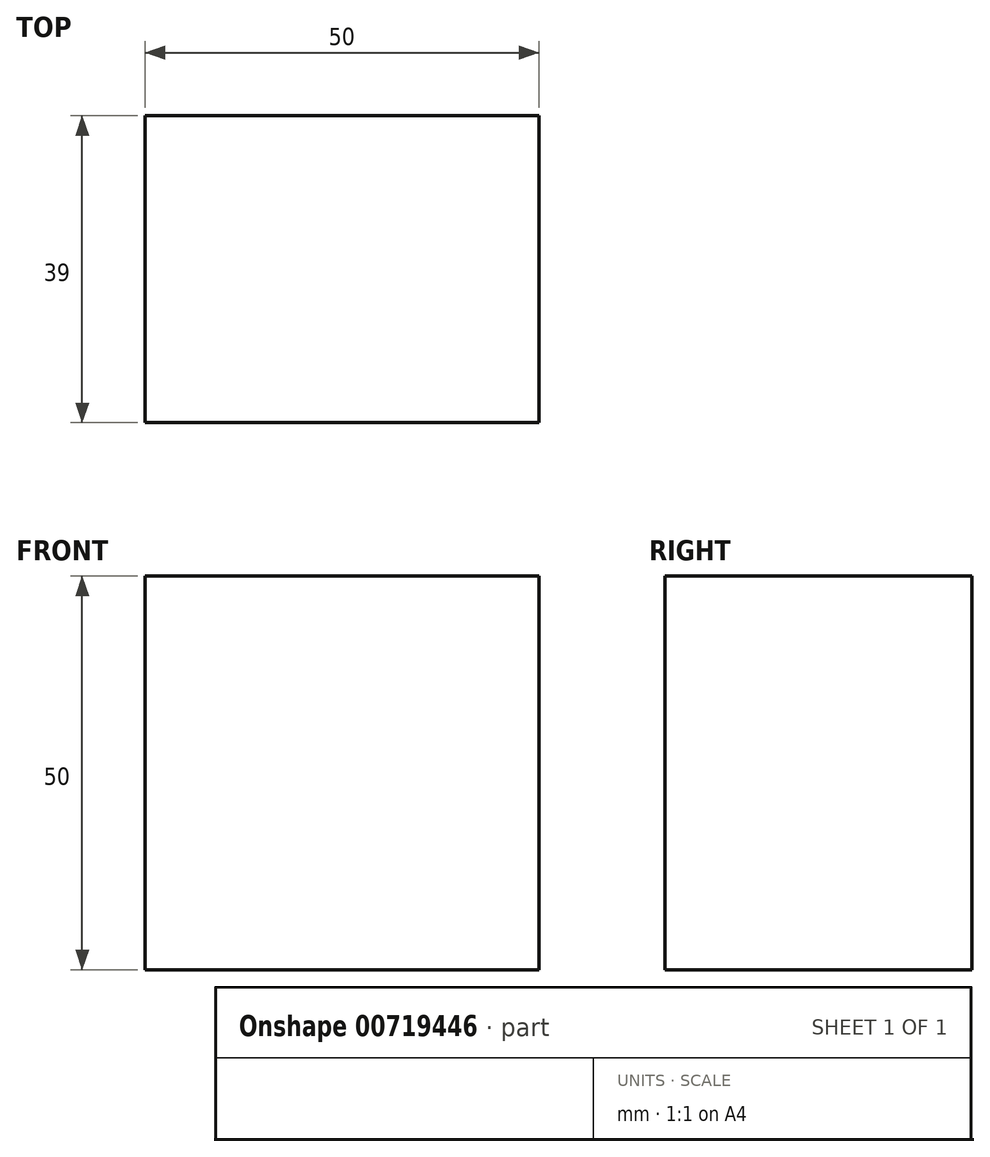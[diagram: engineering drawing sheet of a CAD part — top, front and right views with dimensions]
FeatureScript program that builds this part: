
annotation { "Feature Type Name" : "Feature", "Feature Type Description" : "" }
export const myFeature = defineFeature(function(context is Context, id is Id, definition is map)
    precondition{}
    {
        {
            var Q0;
            Q0=qCreatedBy(makeId("Front.planeOp"),FACE);
            var sketch = newSketch(context, id + "F0", { "sketchPlane" : qUnion([Q0])});
            skLineSegment(sketch, "E0.bottom", {"start": v(-25, 25) * mm, "end": v(25, 25) * mm});
            skLineSegment(sketch, "E0.top", {"start": v(-25, -25) * mm, "end": v(25, -25) * mm});
            skLineSegment(sketch, "E0.left", {"start": v(-25, 25) * mm, "end": v(-25, -25) * mm});
            skLineSegment(sketch, "E0.right", {"start": v(25, 25) * mm, "end": v(25, -25) * mm});
            skSolve(sketch);
        }
        {
            var Q0;
            Q0=makeQuery(id+"F0.imprint","IMPRINT",FACE,{"disambiguationData":[TD([[makeQuery(id+"F0.imprint","IMPRINT",EDGE,{"derivedFrom":sQuery(id+"F0.wireOp",EDGE,"E0.bottom")}),-1.0]])]});
            extrude(context, id + "F1", {"entities" : qUnion([Q0]), "endBound" : BoundingType.SYMMETRIC, "depth" : 39 * mm, "offsetDistance" : 25 * mm});
        }
    });
